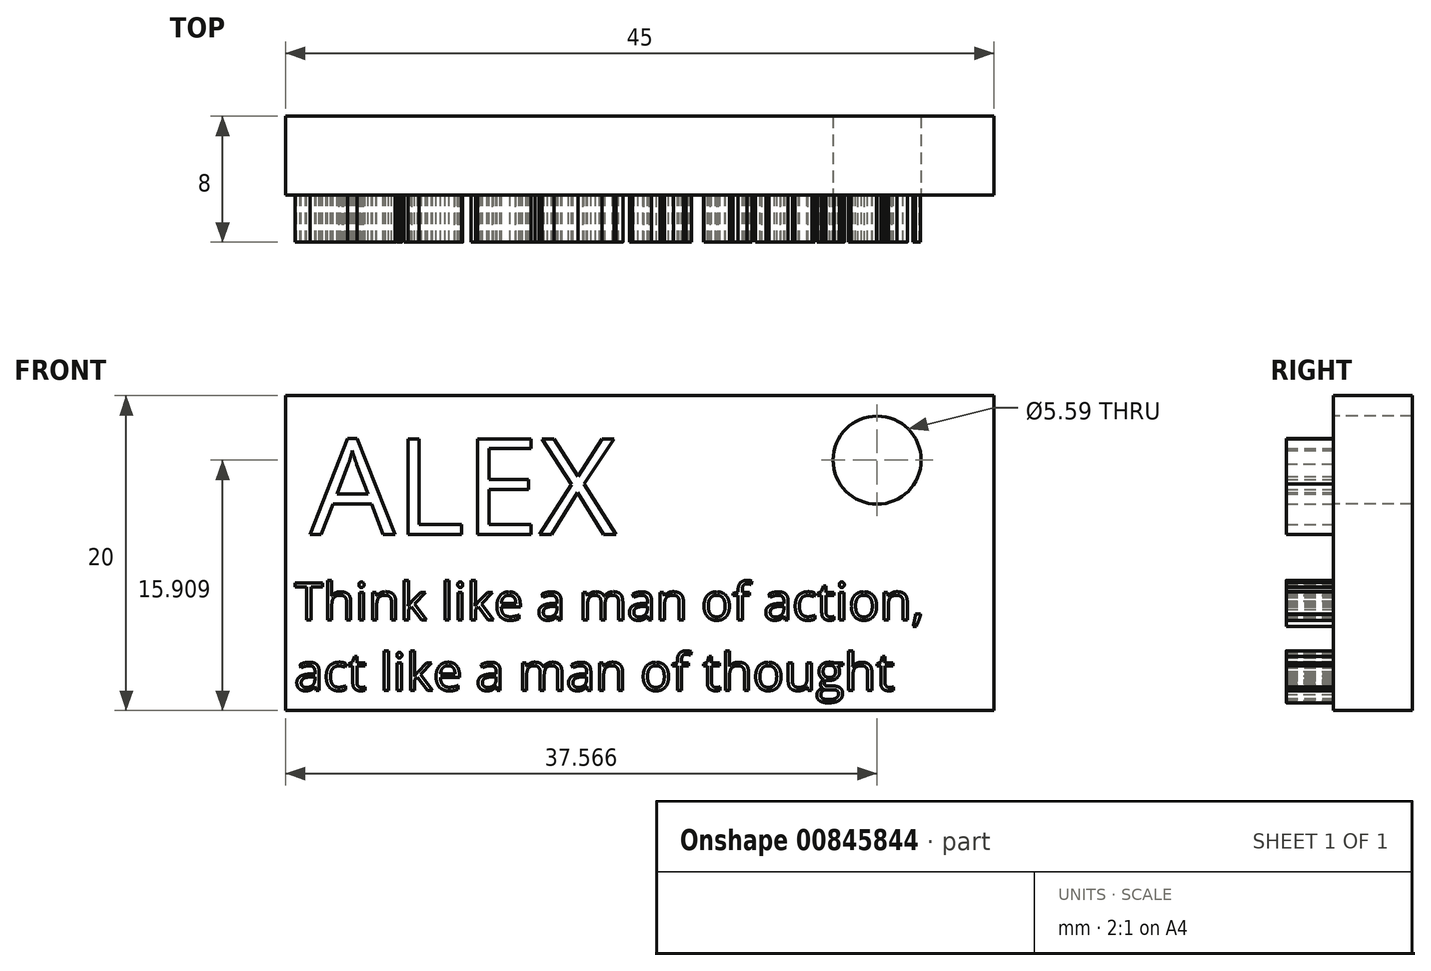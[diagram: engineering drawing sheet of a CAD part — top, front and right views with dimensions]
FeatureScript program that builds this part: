
annotation { "Feature Type Name" : "Feature", "Feature Type Description" : "" }
export const myFeature = defineFeature(function(context is Context, id is Id, definition is map)
    precondition{}
    {
        {
            var Q0;
            Q0=qCreatedBy(makeId("Front.planeOp"),FACE);
            var sketch = newSketch(context, id + "F0", { "sketchPlane" : qUnion([Q0])});
            skLineSegment(sketch, "E0.bottom", {"start": v(0, 0) * mm, "end": v(45, 0) * mm});
            skLineSegment(sketch, "E0.top", {"start": v(0, 20) * mm, "end": v(45, 20) * mm});
            skLineSegment(sketch, "E0.left", {"start": v(0, 0) * mm, "end": v(0, 20) * mm});
            skLineSegment(sketch, "E0.right", {"start": v(45, 0) * mm, "end": v(45, 20) * mm});
            skSolve(sketch);
        }
        {
            var Q0;
            Q0=makeQuery(id+"F0.imprint","IMPRINT",FACE,{"disambiguationData":[TD([[makeQuery(id+"F0.imprint","IMPRINT",EDGE,{"derivedFrom":sQuery(id+"F0.wireOp",EDGE,"E0.bottom")}),1.0]])]});
            extrude(context, id + "F1", {"entities" : qUnion([Q0]), "depth" : 5 * mm, "offsetDistance" : 25 * mm});
        }
        {
            var Q0;
            Q0=makeQuery(id+"F1.opExtrude","CAP_FACE",FACE,{"disambiguationData":[OSD([sQuery(id+"F0.wireOp",EDGE,"E0.bottom"),sQuery(id+"F0.wireOp",EDGE,"E0.top"),sQuery(id+"F0.wireOp",EDGE,"E0.left"),sQuery(id+"F0.wireOp",EDGE,"E0.right")])],"isStart":false});
            var sketch = newSketch(context, id + "F2", { "sketchPlane" : qUnion([Q0])});
            skText(sketch, "E1", { "text": "ALEX", "fontName": "OpenSans-Regular.ttf"});
            const initialGuessF2  = {"E1": [0.00154, 0.01118, 1, 0, 0.00614]};
            skSetInitialGuess(sketch, initialGuessF2);
            skSolve(sketch);
        }
        {
            var Q0;
            Q0 = qSketchRegion(id + "F2", true);
            extrude(context, id + "F3", {"entities" : qUnion([Q0]), "operationType" : NewBodyOperationType.ADD, "depth" : 3 * mm, "offsetDistance" : 25 * mm});
        }
        {
            var Q0;
            {var subQ0=sQuery(id+"F0.wireOp",EDGE,"E0.top");var subQ1=sQuery(id+"F0.wireOp",EDGE,"E0.right");var subQ2=sQuery(id+"F0.wireOp",EDGE,"E0.bottom");var subQ3=sQuery(id+"F0.wireOp",EDGE,"E0.left");Q0=makeQuery(id+"F3.boolean.opBoolean","SPLIT",FACE,{"disambiguationData":[TD([makeQuery(id+"F1.opExtrude","SWEPT_FACE",FACE,{"disambiguationData":[OSD([subQ2])]})])],"derivedFrom":makeQuery(id+"F1.opExtrude","CAP_FACE",FACE,{"disambiguationData":[OSD([subQ2,subQ0,subQ3,subQ1])],"isStart":false})});}
            var sketch = newSketch(context, id + "F4", { "sketchPlane" : qUnion([Q0])});
            skText(sketch, "E2", { "text": "Think like a man of action,\nact like a man of thought", "fontName": "OpenSans-Regular.ttf"});
            const initialGuessF4  = {"E2": [0.00056, 0.00576, 1, 0, 0.00237]};
            skSetInitialGuess(sketch, initialGuessF4);
            skSolve(sketch);
        }
        {
            var Q0;
            Q0 = qSketchRegion(id + "F4", true);
            extrude(context, id + "F5", {"entities" : qUnion([Q0]), "operationType" : NewBodyOperationType.ADD, "depth" : 3 * mm, "offsetDistance" : 25 * mm});
        }
        {
            var Q0;
            {var subQ0=sQuery(id+"F0.wireOp",EDGE,"E0.bottom");var subQ1=makeQuery(id+"F1.opExtrude","SWEPT_FACE",FACE,{"disambiguationData":[OSD([subQ0])]});var subQ3=sQuery(id+"F0.wireOp",EDGE,"E0.right");var subQ6=sQuery(id+"F0.wireOp",EDGE,"E0.left");var subQ10=sQuery(id+"F0.wireOp",EDGE,"E0.top");Q0=makeQuery(id+"F5.boolean.opBoolean","SPLIT",FACE,{"disambiguationData":[TD([subQ1])],"derivedFrom":makeQuery(id+"F3.boolean.opBoolean","SPLIT",FACE,{"disambiguationData":[TD([subQ1])],"derivedFrom":makeQuery(id+"F1.opExtrude","CAP_FACE",FACE,{"disambiguationData":[OSD([subQ0,subQ10,subQ6,subQ3])],"isStart":false})})});}
            var sketch = newSketch(context, id + "F6", { "sketchPlane" : qUnion([Q0])});
            skCircle(sketch, "E3", {"center": v(37.57, 15.9) * mm, "radius": 2.8 * mm});
            skSolve(sketch);
        }
        {
            var Q0;
            Q0=makeQuery(id+"F6.imprint","IMPRINT",FACE,{"disambiguationData":[TD([[makeQuery(id+"F6.imprint","IMPRINT",EDGE,{"derivedFrom":sQuery(id+"F6.wireOp",EDGE,"E3")}),1.0]])]});
            extrude(context, id + "F7", {"entities" : qUnion([Q0]), "operationType" : NewBodyOperationType.REMOVE, "oppositeDirection" : true, "depth" : 25 * mm, "offsetDistance" : 25 * mm});
        }
    });
